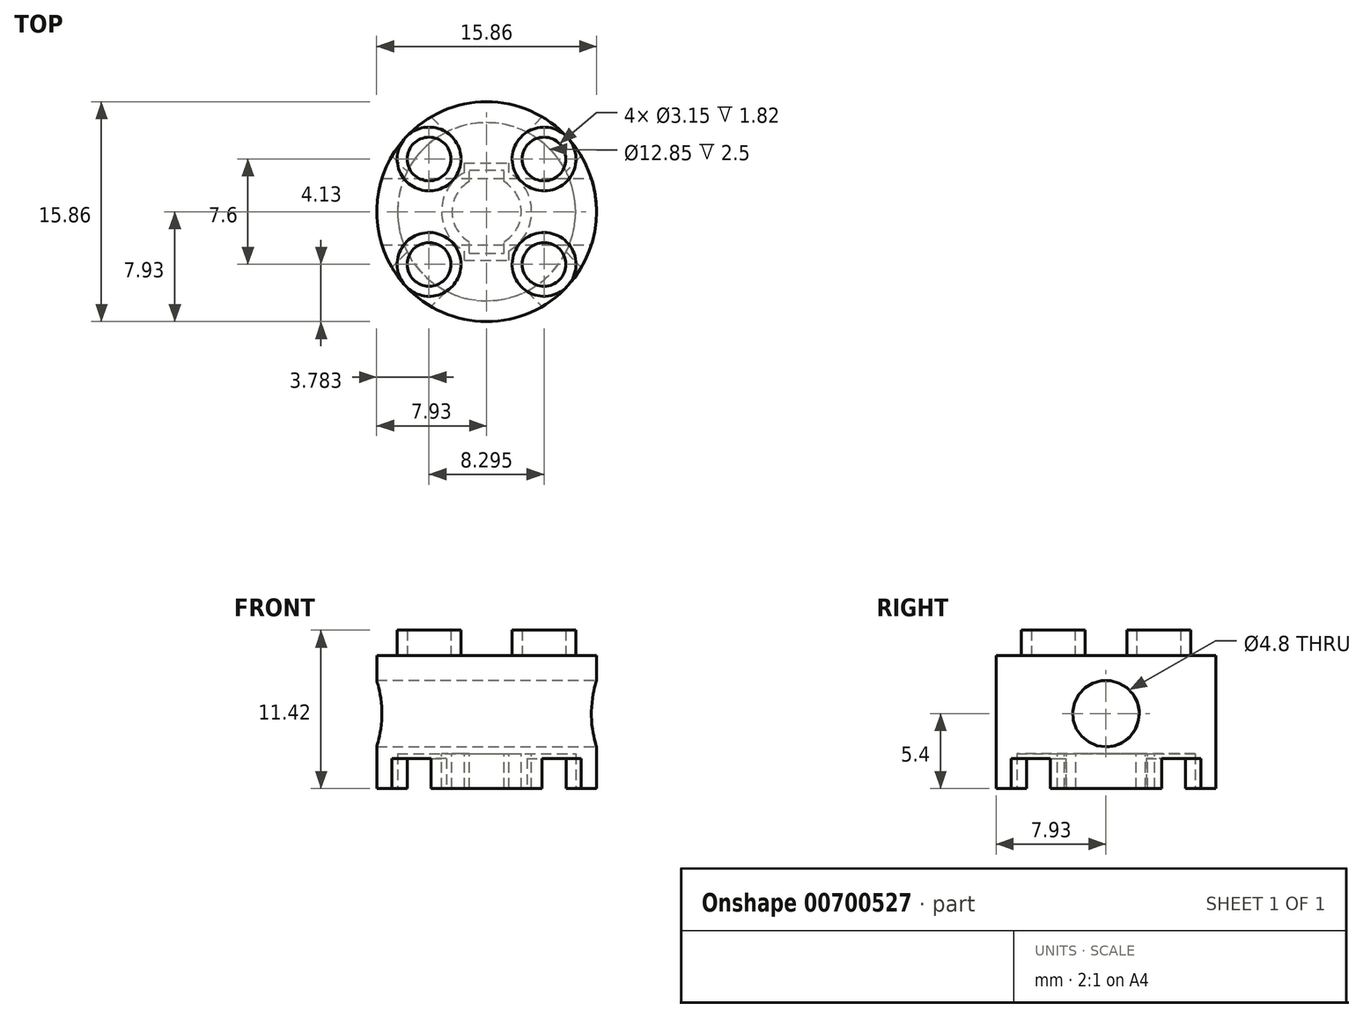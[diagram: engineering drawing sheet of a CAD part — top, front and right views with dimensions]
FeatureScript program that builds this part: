
annotation { "Feature Type Name" : "Feature", "Feature Type Description" : "" }
export const myFeature = defineFeature(function(context is Context, id is Id, definition is map)
    precondition{}
    {
        {
            var Q0;
            Q0=qCreatedBy(makeId("Top.planeOp"),FACE);
            var sketch = newSketch(context, id + "F0", { "sketchPlane" : qUnion([Q0])});
            skCircle(sketch, "E0", {"center": v(0, 0) * mm, "radius": 7.93 * mm});
            skSolve(sketch);
        }
        {
            var Q0;
            Q0 = qSketchRegion(id + "F0", true);
            extrude(context, id + "F1", {"entities" : qUnion([Q0]), "depth" : 9.6 * mm, "offsetDistance" : 25 * mm});
        }
        {
            var Q0;
            Q0=makeQuery(id+"F1.opExtrude","CAP_FACE",FACE,{"disambiguationData":[OSD([sQuery(id+"F0.wireOp",EDGE,"E0")])],"isStart":true});
            var sketch = newSketch(context, id + "F2", { "sketchPlane" : qUnion([Q0])});
            skCircle(sketch, "E1", {"center": v(0, 0) * mm, "radius": 6.43 * mm});
            skSolve(sketch);
        }
        {
            var Q0;
            Q0 = qSketchRegion(id + "F2", true);
            extrude(context, id + "F3", {"entities" : qUnion([Q0]), "operationType" : NewBodyOperationType.REMOVE, "oppositeDirection" : true, "depth" : 2.5 * mm, "offsetDistance" : 25 * mm});
        }
        {
            var Q0;
            Q0=makeQuery(id+"F1.opExtrude","CAP_FACE",FACE,{"disambiguationData":[OSD([sQuery(id+"F0.wireOp",EDGE,"E0")])],"isStart":false});
            var sketch = newSketch(context, id + "F4", { "sketchPlane" : qUnion([Q0])});
            skCircle(sketch, "E2", {"center": v(-4.15, -3.8) * mm, "radius": 2.3 * mm});
            skCircle(sketch, "E3.MirrorC", {"center": v(-4.15, 3.8) * mm, "radius": 2.3 * mm});
            skCircle(sketch, "E4.MirrorC", {"center": v(4.15, 3.8) * mm, "radius": 2.3 * mm});
            skCircle(sketch, "E5.MirrorC", {"center": v(4.15, -3.8) * mm, "radius": 2.3 * mm});
            skCircle(sketch, "E6", {"center": v(-4.15, -3.8) * mm, "radius": 1.57 * mm});
            skCircle(sketch, "E7.MirrorC", {"center": v(-4.15, 3.8) * mm, "radius": 1.57 * mm});
            skCircle(sketch, "E8.MirrorC", {"center": v(4.15, 3.8) * mm, "radius": 1.57 * mm});
            skCircle(sketch, "E9.MirrorC", {"center": v(4.15, -3.8) * mm, "radius": 1.57 * mm});
            skSolve(sketch);
        }
        {
            var Q0;
            Q0 = qSketchRegion(id + "F4", true);
            extrude(context, id + "F5", {"entities" : qUnion([Q0]), "operationType" : NewBodyOperationType.ADD, "depth" : (11.42 - 9.6) * mm, "offsetDistance" : 25 * mm});
        }
        {
            var Q0;
            Q0=qCreatedBy(makeId("Right.planeOp"),FACE);
            cPlane(context, id + "F6", {"entities" : qUnion([Q0]), "cplaneType" : CPlaneType.OFFSET, "offset" : (15.85 / 2) * mm, "width" : 150 * mm, "height" : 150 * mm});
        }
        {
            var Q0;
            Q0=qCreatedBy(makeId("Front.planeOp"),FACE);
            cPlane(context, id + "F7", {"entities" : qUnion([Q0]), "cplaneType" : CPlaneType.OFFSET, "offset" : (15.85 / 2) * mm, "width" : 150 * mm, "height" : 150 * mm});
        }
        {
            var Q0;
            Q0=qCreatedBy(id+"F6.planeOp",FACE);
            var Q1;
            Q1=qCreatedBy(id+"F7.planeOp",FACE);
            cPlane(context, id + "F8", {"entities" : qUnion([Q0, Q1]), "cplaneType" : CPlaneType.MID_PLANE, "offset" : 25 * mm, "flipAlignment" : true, "width" : 150 * mm, "height" : 150 * mm});
        }
        {
            var Q0;
            Q0=qCreatedBy(id+"F7.planeOp",FACE);
            cPlane(context, id + "F9", {"entities" : qUnion([Q0]), "cplaneType" : CPlaneType.OFFSET, "offset" : 15.85 * mm, "oppositeDirection" : true, "width" : 150 * mm, "height" : 150 * mm});
        }
        {
            var Q0;
            Q0=qCreatedBy(id+"F8.planeOp",FACE);
            var sketch = newSketch(context, id + "F10", { "sketchPlane" : qUnion([Q0])});
            skLineSegment(sketch, "E10.bottom", {"start": v(2, 2.17) * mm, "end": v(-2, 2.17) * mm});
            skLineSegment(sketch, "E10.top", {"start": v(2, -2.17) * mm, "end": v(-2, -2.17) * mm});
            skLineSegment(sketch, "E10.left", {"start": v(2, 2.17) * mm, "end": v(2, -2.17) * mm});
            skLineSegment(sketch, "E10.right", {"start": v(-2, 2.17) * mm, "end": v(-2, -2.17) * mm});
            skPoint(sketch, "E10.middle", {"position": v(0, 0) * mm});
            skSolve(sketch);
        }
        {
            var Q0;
            Q0=qCreatedBy(id+"F6.planeOp",FACE);
            var Q1;
            Q1=qCreatedBy(id+"F9.planeOp",FACE);
            cPlane(context, id + "F11", {"entities" : qUnion([Q0, Q1]), "cplaneType" : CPlaneType.MID_PLANE, "offset" : 25 * mm, "width" : 150 * mm, "height" : 150 * mm});
        }
        {
            var Q0;
            Q0=qCreatedBy(id+"F11.planeOp",FACE);
            var sketch = newSketch(context, id + "F12", { "sketchPlane" : qUnion([Q0])});
            skLineSegment(sketch, "E11.bottom", {"start": v(-2, -2.17) * mm, "end": v(2, -2.17) * mm});
            skLineSegment(sketch, "E11.top", {"start": v(-2, 2.17) * mm, "end": v(2, 2.17) * mm});
            skLineSegment(sketch, "E11.left", {"start": v(-2, -2.17) * mm, "end": v(-2, 2.17) * mm});
            skLineSegment(sketch, "E11.right", {"start": v(2, -2.17) * mm, "end": v(2, 2.17) * mm});
            skPoint(sketch, "E11.middle", {"position": v(0, 0) * mm});
            skSolve(sketch);
        }
        {
            var Q0;
            Q0 = qSketchRegion(id + "F12", true);
            extrude(context, id + "F13", {"entities" : qUnion([Q0]), "operationType" : NewBodyOperationType.REMOVE, "endBound" : BoundingType.THROUGH_ALL, "oppositeDirection" : true, "depth" : 25 * mm, "offsetDistance" : 25 * mm});
        }
        {
            var Q0;
            Q0=makeQuery(id+"F10.imprint","IMPRINT",FACE,{"disambiguationData":[TD([[makeQuery(id+"F10.imprint","IMPRINT",EDGE,{"derivedFrom":sQuery(id+"F10.wireOp",EDGE,"E10.bottom")}),1.0]])]});
            extrude(context, id + "F14", {"entities" : qUnion([Q0]), "operationType" : NewBodyOperationType.REMOVE, "endBound" : BoundingType.THROUGH_ALL, "oppositeDirection" : true, "depth" : 25 * mm, "offsetDistance" : 25 * mm});
        }
        {
            var Q0;
            Q0=qCreatedBy(id+"F6.planeOp",FACE);
            var sketch = newSketch(context, id + "F15", { "sketchPlane" : qUnion([Q0])});
            skCircle(sketch, "E12", {"center": v(0, 5.4) * mm, "radius": 2.4 * mm});
            skSolve(sketch);
        }
        {
            var Q0;
            {var subQ0=sQuery(id+"F0.wireOp",EDGE,"E0");Q0=makeQuery(id+"F5.boolean.opBoolean","SPLIT",FACE,{"disambiguationData":[TD([makeQuery(id+"F1.opExtrude","SWEPT_FACE",FACE,{"disambiguationData":[OSD([subQ0])]})])],"derivedFrom":makeQuery(id+"F1.opExtrude","CAP_FACE",FACE,{"disambiguationData":[OSD([subQ0])],"isStart":false})});}
            var sketch = newSketch(context, id + "F16", { "sketchPlane" : qUnion([Q0])});
            skLineSegment(sketch, "E13.bottom", {"start": v(1.6, 3.5) * mm, "end": v(-1.6, 3.5) * mm});
            skLineSegment(sketch, "E13.top", {"start": v(1.6, -3.5) * mm, "end": v(-1.6, -3.5) * mm});
            skLineSegment(sketch, "E13.left", {"start": v(1.6, 3.5) * mm, "end": v(1.6, -3.5) * mm});
            skLineSegment(sketch, "E13.right", {"start": v(-1.6, 3.5) * mm, "end": v(-1.6, -3.5) * mm});
            skPoint(sketch, "E13.middle", {"position": v(0, 0) * mm});
            skCircle(sketch, "E14", {"center": v(0, 0) * mm, "radius": 2.5 * mm});
            skLineSegment(sketch, "E15.bottom", {"start": v(1.25, 3) * mm, "end": v(-1.25, 3) * mm});
            skLineSegment(sketch, "E15.top", {"start": v(1.25, -3) * mm, "end": v(-1.25, -3) * mm});
            skLineSegment(sketch, "E15.left", {"start": v(1.25, 3) * mm, "end": v(1.25, -3) * mm});
            skLineSegment(sketch, "E15.right", {"start": v(-1.25, 3) * mm, "end": v(-1.25, -3) * mm});
            skCircle(sketch, "E16", {"center": v(0, 0) * mm, "radius": 3.25 * mm});
            skSolve(sketch);
        }
        {
            var Q0;
            Q0 = qSketchRegion(id + "F16", true);
            var Q1;
            {var subQ0=sQuery(id+"F16.wireOp",EDGE,"E15.bottom");Q1=makeQuery(id+"F16.imprint","IMPRINT",FACE,{"disambiguationData":[TD([[makeQuery(id+"F16.imprint","IMPRINT",EDGE,{"derivedFrom":subQ0}),-1.0]])]});}
            var Q2;
            {var subQ0=sQuery(id+"F16.wireOp",EDGE,"E15.top");Q2=makeQuery(id+"F16.imprint","IMPRINT",FACE,{"disambiguationData":[TD([[makeQuery(id+"F16.imprint","IMPRINT",EDGE,{"derivedFrom":subQ0}),1.0]])]});}
            extrude(context, id + "F17", {"entities" : qUnion([Q0, Q1, Q2]), "operationType" : NewBodyOperationType.ADD, "oppositeDirection" : true, "depth" : 9.6 * mm, "offsetDistance" : 25 * mm});
        }
        {
            var Q0;
            Q0=makeQuery(id+"F15.imprint","IMPRINT",FACE,{"disambiguationData":[TD([[makeQuery(id+"F15.imprint","IMPRINT",EDGE,{"derivedFrom":sQuery(id+"F15.wireOp",EDGE,"E12")}),1.0]])]});
            extrude(context, id + "F18", {"entities" : qUnion([Q0]), "operationType" : NewBodyOperationType.REMOVE, "endBound" : BoundingType.THROUGH_ALL, "oppositeDirection" : true, "depth" : 25 * mm, "offsetDistance" : 25 * mm});
        }
    });
